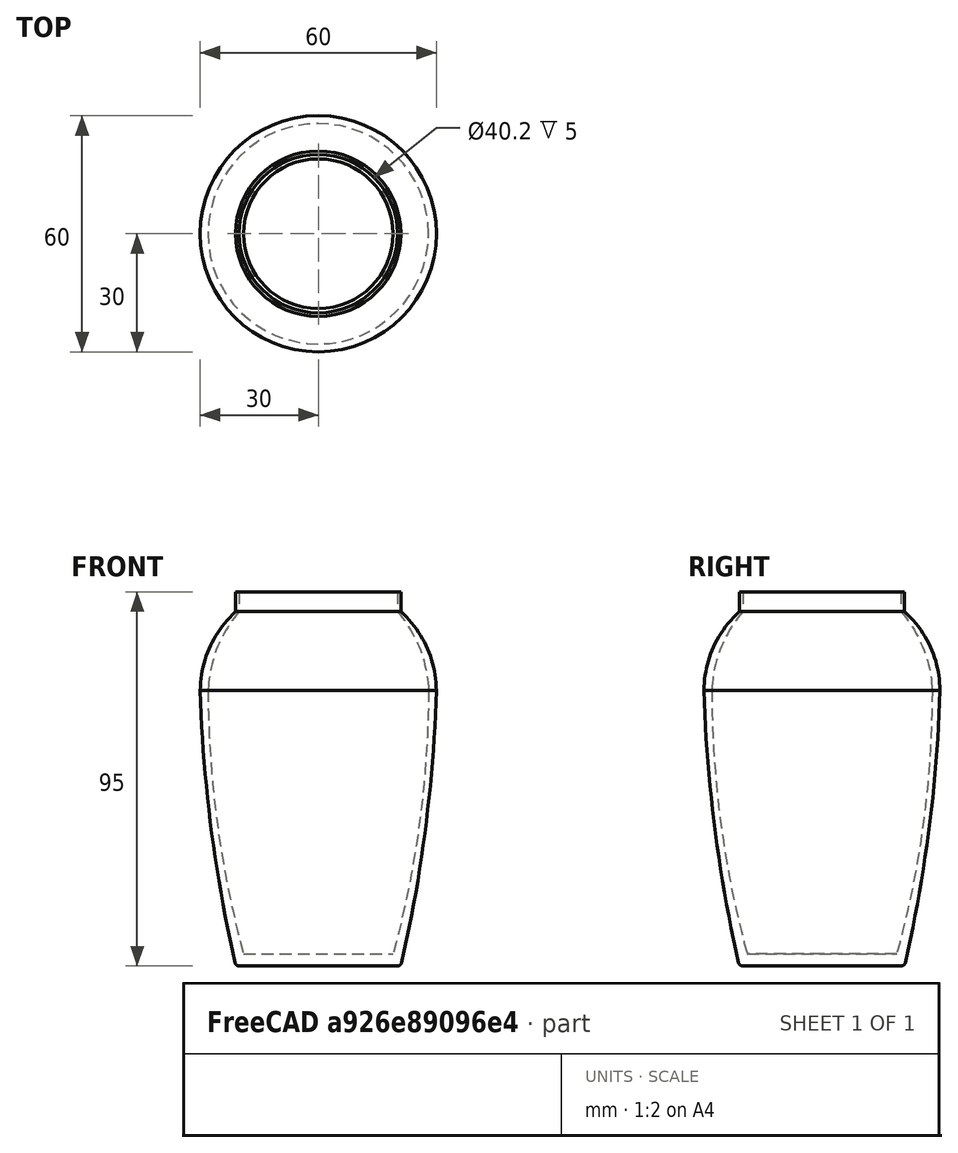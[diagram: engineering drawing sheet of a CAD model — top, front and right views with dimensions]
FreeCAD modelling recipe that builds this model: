
FCSTD DOCUMENT  (FreeCAD 0.20R29410 (Git))
Label: cup2
License: All rights reserved
LicenseURL: http://en.wikipedia.org/wiki/All_rights_reserved
objects: Part::Part2DObjectPython×12, Part::Feature×2, App::DocumentObjectGroup×2, Part::Revolution×2, Part::Cut×1, Part::Fillet×1
note: 18 computed .brp shape members not serialized (recipe doc carries the construction recipe); baked Part::Feature solids carry a one-line shape summary decoded from their .brp

FEATURE [Part::Part2DObjectPython] Line001  # Draft 2D object (typed FeaturePython)
  Area = 0
  ChamferSize = 0
  Closed = false
  End = (-21,0,-1.3e-15)
  FilletRadius = 0
  Length = 21
  MakeFace = true
  Placement = pos=(0,0,0) rot=(1,0,0;1.5708rad)
  Points = (2) [(0,0,0),(-21,-6.4294e-16,6.4294e-16)]
  Start = (0,0,0)
  Subdivisions = 0
FEATURE [Part::Part2DObjectPython] BSpline002  # Draft 2D object (typed FeaturePython)
  Area = 0
  Closed = false
  MakeFace = true
  Parameterization = 1
  Points = (3) [(-30,0,70),(-25,0,20),(-21,0,-1.28588e-15)]
FEATURE [Part::Part2DObjectPython] Line003  # Draft 2D object (typed FeaturePython)
  Area = 0
  ChamferSize = 0
  Closed = false
  End = (-21,0,95)
  FilletRadius = 0
  Length = 5
  MakeFace = true
  Placement = pos=(-22,0,90) rot=(1,0,0;1.5708rad)
  Points = (2) [(1,0,-3.06162e-17),(1,5,1.07961e-15)]
  Start = (-21,0,90)
  Subdivisions = 0
FEATURE [Part::Part2DObjectPython] Line004  # Draft 2D object (typed FeaturePython)
  Area = 0
  ChamferSize = 0
  Closed = false
  End = (0,0,95)
  FilletRadius = 0
  Length = 21
  MakeFace = true
  Placement = pos=(-22,0,95) rot=(1,0,0;1.5708rad)
  Points = (2) [(1,0,-3.06162e-17),(22,0,-6.73556e-16)]
  Start = (-21,0,95)
  Subdivisions = 0
FEATURE [Part::Part2DObjectPython] Line005  # Draft 2D object (typed FeaturePython)
  Area = 0
  ChamferSize = 0
  Closed = false
  End = (0,0,0)
  FilletRadius = 0
  Length = 95
  MakeFace = true
  Placement = pos=(0,0,95) rot=(1,0,0;1.5708rad)
  Points = (2) [(0,0,0),(-2.90854e-15,-95,-2.10942e-14)]
  Start = (0,0,95)
  Subdivisions = 0
FEATURE [Part::Part2DObjectPython] Line  # Draft 2D object (typed FeaturePython)
  Area = 0
  ChamferSize = 0
  Closed = false
  End = (-20.1,0,95)
  FilletRadius = 0
  Length = 20.1
  MakeFace = true
  Placement = pos=(0,0,95) rot=(1,0,0;1.5708rad)
  Points = (2) [(0,0,0),(-20.1,0,6.15385e-16)]
  Start = (0,0,95)
  Subdivisions = 0
FEATURE [Part::Part2DObjectPython] Line006  # Draft 2D object (typed FeaturePython)
  Area = 0
  ChamferSize = 0
  Closed = false
  End = (-20.1,0,90)
  FilletRadius = 0
  Length = 5
  MakeFace = true
  Placement = pos=(-20.1,0,95) rot=(1,0,0;1.5708rad)
  Points = (2) [(0,0,0),(0,-5,-1.11022e-15)]
  Start = (-20.1,0,95)
  Subdivisions = 0
FEATURE [Part::Part2DObjectPython] BSpline  # Draft 2D object (typed FeaturePython)
  Area = 0
  Closed = false
  MakeFace = true
  Parameterization = 1
  Points = (3) [(-21,-3.69779e-32,90),(-28,0,80),(-30,0,70)]
FEATURE [Part::Part2DObjectPython] BSpline003  # Draft 2D object (typed FeaturePython)
  Area = 0
  Closed = false
  MakeFace = true
  Parameterization = 1
  Points = (3) [(-20.1,4.93038e-31,90),(-26,0,80),(-28,0,70)]
FEATURE [Part::Part2DObjectPython] BSpline004  # Draft 2D object (typed FeaturePython)
  Area = 0
  Closed = false
  MakeFace = true
  Parameterization = 1
  Points = (3) [(-28,0,70),(-23,0,20),(-19,0,3)]
FEATURE [Part::Part2DObjectPython] Line007  # Draft 2D object (typed FeaturePython)
  Area = 0
  ChamferSize = 0
  Closed = false
  End = (0,0,3)
  FilletRadius = 0
  Length = 19
  MakeFace = true
  Placement = pos=(-19,0,3) rot=(1,0,0;1.5708rad)
  Points = (2) [(0,0,0),(19,8.88178e-16,-5.81707e-16)]
  Start = (-19,0,3)
  Subdivisions = 0
FEATURE [Part::Part2DObjectPython] Line008  # Draft 2D object (typed FeaturePython)
  Area = 0
  ChamferSize = 0
  Closed = false
  End = (0,0,3)
  FilletRadius = 0
  Length = 92
  MakeFace = true
  Placement = pos=(0,0,95) rot=(1,0,0;1.5708rad)
  Points = (2) [(0,0,0),(-2.81669e-15,-92,-2.04281e-14)]
  Start = (0,0,95)
  Subdivisions = 0
FEATURE [Part::Feature] Face
  shape: bbox 41.67 x 2e-07 x 107.8 mm, 1 faces, 0 solids (baked)
FEATURE [App::DocumentObjectGroup] ____________001  label="外壁"
  Group = -> [Face,BSpline002,Line004,Line001,BSpline,Line005,Line003]
FEATURE [Part::Revolution] Revolve
  Angle = 360
  Axis = (0,0,1)
  Base = (0,0,0)
  FaceMakerClass = Part::FaceMakerBullseye
  Solid = true
  Source = -> Face
  Symmetric = false
FEATURE [Part::Feature] Face001
  shape: bbox 39.88 x 2e-07 x 104.4 mm, 1 faces, 0 solids (baked)
FEATURE [Part::Revolution] Revolve001
  Angle = 360
  Axis = (0,0,1)
  Base = (0,0,0)
  FaceMakerClass = Part::FaceMakerBullseye
  Solid = true
  Source = -> Face001
  Symmetric = false
FEATURE [Part::Cut] Cut  label="少し余裕あり、短め"
  Base = -> Revolve
  Tool = -> Revolve001
FEATURE [App::DocumentObjectGroup] ____________  label="内壁"
  Group = -> [Line,Face001,BSpline004,Line007,Line008,Line006,BSpline003,Cut]
FEATURE [Part::Fillet] Fillet
  Base = -> Cut
  Edges = 1 edges r=1: [Edge1]
